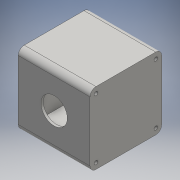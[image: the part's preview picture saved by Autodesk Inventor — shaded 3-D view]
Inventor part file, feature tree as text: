
AUTODESK INVENTOR PART (.ipt)
format: ipt  version: 2016 (Build 200138000, 138)  size: 155,136 bytes
history: native  units: mm
features: extrude x5, sketch x5, fillet x1
ambient origin geometry x8: Origin, YZ Plane, XZ Plane, XY Plane, X Axis, Y Axis, Z Axis, Center Point
bodies: Solid1 (feature_tree)
feature tree (11):
  extrude  "Main Block"  Depth=60.0mm
  extrude  "Motor Void"  Depth=42.5mm
  extrude  "Cable Void"  Depth=58.0mm TaperAngle=0.0deg
  extrude  "Raised Void"  Depth=41.0mm
  extrude  "Holes"  Depth=16.5mm
  fillet  "Cleaning it up"  Radius=9.0mm
  sketch  "Sketch1"  dims[d0=60.0mm d1=60.0mm]
  sketch  "Sketch2"  dims[d2=60.0mm d3=0.0mm d4=42.5mm]
  sketch  "Sketch3"  dims[d5=42.5mm d6=58.0mm d7=0.0mm]
  sketch  "Sketch4"  dims[d10=41.0mm d11=0.0mm d12=22.0mm]
  sketch  "Sketch6"  dims[d13=2.0mm d14=0.0mm d30=16.5mm d31=9.0mm d32=5.0mm d33=5.0mm d34=5.0mm d35=5.0mm d36=5.0mm d37=5.0mm d38=5.0mm d39=5.0mm d40=3.0mm d41=3.0mm d42=3.0mm d43=3.0mm d44=60.0mm d45=0.0mm d46=5.0mm]
